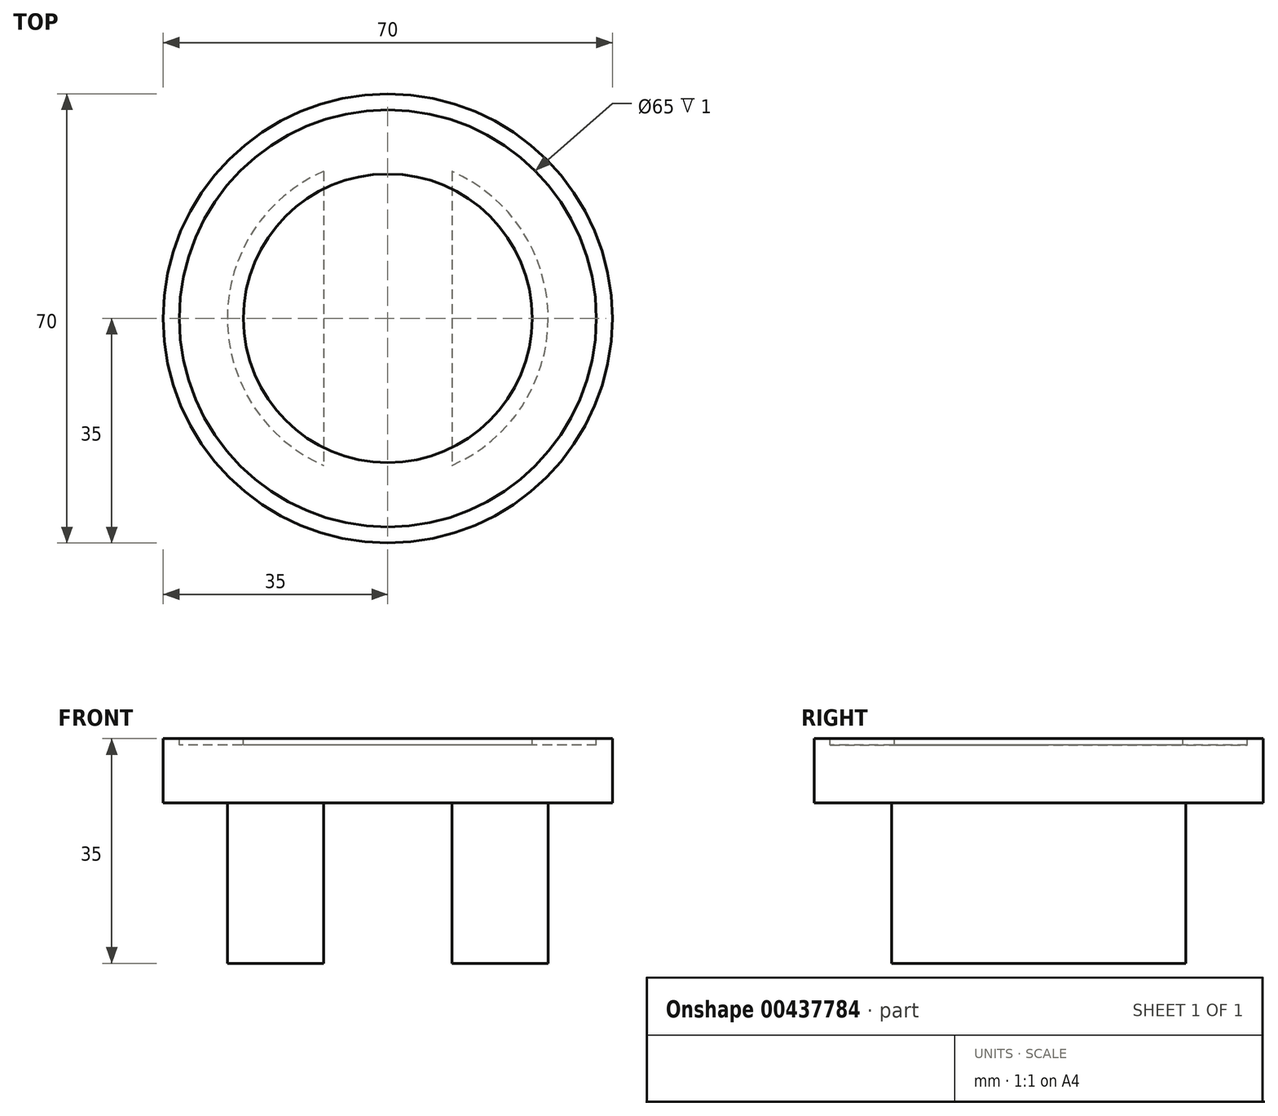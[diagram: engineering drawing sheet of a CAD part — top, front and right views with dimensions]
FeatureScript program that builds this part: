
annotation { "Feature Type Name" : "Feature", "Feature Type Description" : "" }
export const myFeature = defineFeature(function(context is Context, id is Id, definition is map)
    precondition{}
    {
        {
            var Q0;
            Q0=qCreatedBy(makeId("Top.planeOp"),FACE);
            var sketch = newSketch(context, id + "F0", { "sketchPlane" : qUnion([Q0])});
            skCircle(sketch, "E0", {"center": v(0, 0) * mm, "radius": 35 * mm});
            skSolve(sketch);
        }
        {
            var Q0;
            Q0 = qSketchRegion(id + "F0", true);
            extrude(context, id + "F1", {"entities" : qUnion([Q0]), "depth" : 10 * mm});
        }
        {
            var Q0;
            Q0=qCreatedBy(makeId("Top.planeOp"),FACE);
            var sketch = newSketch(context, id + "F2", { "sketchPlane" : qUnion([Q0])});
            skCircle(sketch, "E1", {"center": v(0, 0) * mm, "radius": 25 * mm});
            skSolve(sketch);
        }
        {
            var Q0;
            Q0 = qSketchRegion(id + "F2", true);
            extrude(context, id + "F3", {"entities" : qUnion([Q0]), "operationType" : NewBodyOperationType.ADD, "oppositeDirection" : true, "depth" : 25 * mm});
        }
        {
            var Q0;
            Q0=qCreatedBy(makeId("Top.planeOp"),FACE);
            var sketch = newSketch(context, id + "F4", { "sketchPlane" : qUnion([Q0])});
            skLineSegment(sketch, "E2.bottom", {"start": v(-10, 40) * mm, "end": v(10, 40) * mm});
            skLineSegment(sketch, "E2.top", {"start": v(-10, -40) * mm, "end": v(10, -40) * mm});
            skLineSegment(sketch, "E2.left", {"start": v(-10, 40) * mm, "end": v(-10, -40) * mm});
            skLineSegment(sketch, "E2.right", {"start": v(10, 40) * mm, "end": v(10, -40) * mm});
            skPoint(sketch, "E2.middle", {"position": v(0, 0) * mm});
            skSolve(sketch);
        }
        {
            var Q0;
            Q0 = qSketchRegion(id + "F4", true);
            extrude(context, id + "F5", {"entities" : qUnion([Q0]), "operationType" : NewBodyOperationType.REMOVE, "oppositeDirection" : true, "depth" : 25 * mm});
        }
        {
            var Q0;
            Q0=qCreatedBy(makeId("Top.planeOp"),FACE);
            cPlane(context, id + "F6", {"entities" : qUnion([Q0]), "cplaneType" : CPlaneType.OFFSET, "offset" : 10 * mm, "width" : 150 * mm, "height" : 150 * mm});
        }
        {
            var Q0;
            Q0=qCreatedBy(id+"F6.planeOp",FACE);
            var sketch = newSketch(context, id + "F7", { "sketchPlane" : qUnion([Q0])});
            skCircle(sketch, "E3", {"center": v(0, 0) * mm, "radius": 32.5 * mm});
            skCircle(sketch, "E4", {"center": v(0, 0) * mm, "radius": 22.5 * mm});
            skSolve(sketch);
        }
        {
            var Q0;
            Q0 = qSketchRegion(id + "F7", true);
            extrude(context, id + "F8", {"entities" : qUnion([Q0]), "operationType" : NewBodyOperationType.REMOVE, "oppositeDirection" : true, "depth" : 1 * mm});
        }
    });
